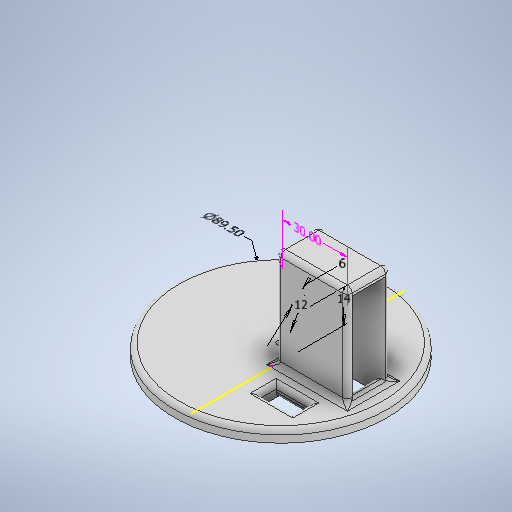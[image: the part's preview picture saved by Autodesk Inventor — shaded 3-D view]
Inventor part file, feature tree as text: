
AUTODESK INVENTOR PART (.ipt)
format: ipt  version: 2025.2 (Build 292293000, 293)  size: 674,816 bytes
history: native  units: mm
features: extrude x11, sketch x11, other x4, fillet x3
ambient origin geometry x8: Origin, YZ Plane, XZ Plane, XY Plane, X Axis, Y Axis, Z Axis, Center Point
bodies: Body1 (feature_tree)
feature tree (29):
  other  "Bryła1"
  other  "Opisy"
  extrude  "Wyciągnięcie proste1"  Depth=89.5mm
  extrude  "Wyciągnięcie proste2"  Depth=5.0mm TaperAngle=0.0deg
  extrude  "Wyciągnięcie proste3"  Depth=36.0mm
  extrude  "Wyciągnięcie proste4"  Depth=7.5mm
  extrude  "Wyciągnięcie proste5"  Depth=4.0mm
  fillet  "Zaokrąglenie1"  Radius=17.0mm
  sketch  "Szkic6"
  extrude  "Wyciągnięcie proste6"  Depth=2.0mm TaperAngle=0.0deg
  extrude  "Wyciągnięcie proste7"  Depth=3.0mm
  extrude  "Wyciągnięcie proste8"  Depth=5.0mm TaperAngle=0.0deg
  extrude  "Wyciągnięcie proste9"  Depth=30.0mm
  extrude  "Wyciągnięcie proste10"  Depth=18.0mm
  fillet  "Zaokrąglenie2"  Radius=37.0mm
  extrude  "Wyciągnięcie proste11"  Depth=42.0mm TaperAngle=0.0deg
  fillet  "Zaokrąglenie3"  Radius=42.0mm
  sketch  "Szkic1"
  sketch  "Szkic2"
  sketch  "Szkic3"
  sketch  "Szkic4"
  sketch  "Szkic5"
  sketch  "Szkic7"
  sketch  "Szkic8"
  sketch  "Szkic9"
  sketch  "Szkic10"
  sketch  "Szkic11"
  other  "Wymiar liniowy 1"
  other  "Wymiar średnicy 1"
